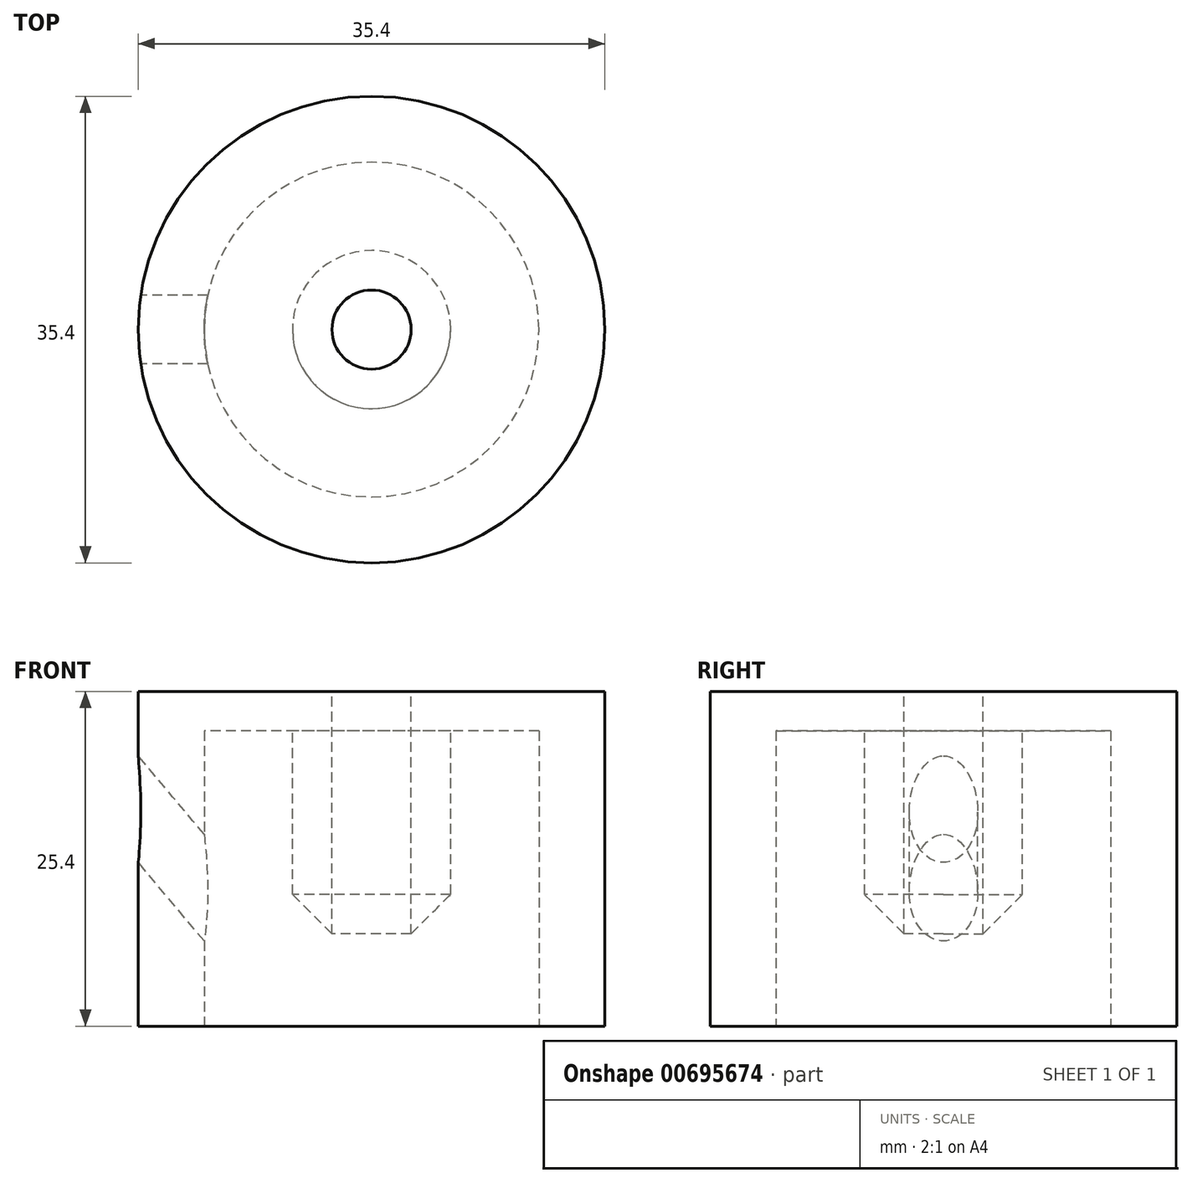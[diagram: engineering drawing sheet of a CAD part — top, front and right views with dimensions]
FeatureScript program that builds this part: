
annotation { "Feature Type Name" : "Feature", "Feature Type Description" : "" }
export const myFeature = defineFeature(function(context is Context, id is Id, definition is map)
    precondition{}
    {
        {
            var Q0;
            Q0=qCreatedBy(makeId("Top.planeOp"),FACE);
            var sketch = newSketch(context, id + "F0", { "sketchPlane" : qUnion([Q0])});
            skCircle(sketch, "E0", {"center": v(0, 0) * mm, "radius": 12.7 * mm});
            skCircle(sketch, "E1", {"center": v(0, 0) * mm, "radius": 17.7 * mm});
            skSolve(sketch);
        }
        {
            var Q0;
            Q0=qSketchRegion(id+"F0",true);
            extrude(context, id + "F1", {"entities" : qUnion([Q0]), "depth" : 25.4 * mm, "offsetDistance" : 25 * mm});
        }
        {
            var Q0;
            Q0=qCreatedBy(makeId("Front.planeOp"),FACE);
            var sketch = newSketch(context, id + "F2", { "sketchPlane" : qUnion([Q0])});
            skLineSegment(sketch, "E2", {"start": v(-34.24, 36.18) * mm, "end": v(-10.1, 7.4) * mm, "construction": true});
            skSolve(sketch);
        }
        {
            var Q0;
            Q0=sQuery(id+"F2.wireOp",EDGE,"E2");
            var Q1;
            Q1=sQuery(id+"F2.wireOp",VERTEX,"E2.start");
            cPlane(context, id + "F3", {"entities" : qUnion([Q0, Q1]), "cplaneType" : CPlaneType.CURVE_POINT, "offset" : 25 * mm, "width" : 150 * mm, "height" : 150 * mm});
        }
        {
            var Q0;
            Q0=qCreatedBy(id+"F3.planeOp",FACE);
            var sketch = newSketch(context, id + "F4", { "sketchPlane" : qUnion([Q0])});
            skCircle(sketch, "E3", {"center": v(-2.97, 0) * mm, "radius": 2.6 * mm});
            skSolve(sketch);
        }
        {
            var Q0;
            Q0=qSketchRegion(id+"F4",true);
            extrude(context, id + "F5", {"entities" : qUnion([Q0]), "operationType" : NewBodyOperationType.REMOVE, "depth" : 38 * mm, "offsetDistance" : 25 * mm});
        }
        {
            var Q0;
            Q0=qCreatedBy(makeId("Front.planeOp"),FACE);
            var sketch = newSketch(context, id + "F6", { "sketchPlane" : qUnion([Q0])});
            skLineSegment(sketch, "E4", {"start": v(0, 87.46) * mm, "end": v(0, -20.33) * mm, "construction": true});
            skSolve(sketch);
        }
        {
            var Q0;
            Q0=makeQuery(id+"F1.opExtrude","CAP_FACE",FACE,{"disambiguationData":[OSD([sQuery(id+"F0.wireOp",EDGE,"E0"),sQuery(id+"F0.wireOp",EDGE,"E1")])],"isStart":true});
            cPlane(context, id + "F7", {"entities" : qUnion([Q0]), "cplaneType" : CPlaneType.OFFSET, "offset" : 10 * mm, "oppositeDirection" : true, "width" : 150 * mm, "height" : 150 * mm});
        }
        {
            var Q0;
            Q0=qCreatedBy(id+"F7.planeOp",FACE);
            var sketch = newSketch(context, id + "F8", { "sketchPlane" : qUnion([Q0])});
            skCircle(sketch, "E5", {"center": v(0, 0) * mm, "radius": 6 * mm});
            skCircle(sketch, "E6", {"center": v(0, 0) * mm, "radius": 3 * mm});
            skSolve(sketch);
        }
        {
            var Q0;
            Q0=qSketchRegion(id+"F8",true);
            extrude(context, id + "F9", {"entities" : qUnion([Q0]), "depth" : 3 * mm, "offsetDistance" : 25 * mm});
        }
        {
            var Q0;
            Q0=makeQuery(id+"F9.opExtrude","CAP_FACE",FACE,{"disambiguationData":[OSD([sQuery(id+"F8.wireOp",EDGE,"E5")])],"isStart":false});
            var sketch = newSketch(context, id + "F10", { "sketchPlane" : qUnion([Q0])});
            skSolve(sketch);
        }
        {
            var Q0;
            Q0=qSketchRegion(id+"F8",true);
            var Q1;
            Q1=makeQuery(id+"F1.opExtrude","CAP_FACE",FACE,{"disambiguationData":[OSD([sQuery(id+"F0.wireOp",EDGE,"E0"),sQuery(id+"F0.wireOp",EDGE,"E1")])],"isStart":false});
            extrude(context, id + "F11", {"entities" : qUnion([Q0]), "operationType" : NewBodyOperationType.ADD, "endBound" : BoundingType.UP_TO_SURFACE, "oppositeDirection" : true, "depth" : 25 * mm, "endBoundEntityFace" : qUnion([Q1]), "offsetDistance" : 25 * mm});
        }
        {
            var Q0;
            Q0=makeQuery(id+"F1.opExtrude","CAP_FACE",FACE,{"disambiguationData":[OSD([sQuery(id+"F0.wireOp",EDGE,"E0"),sQuery(id+"F0.wireOp",EDGE,"E1")])],"isStart":false});
            var sketch = newSketch(context, id + "F12", { "sketchPlane" : qUnion([Q0])});
            skCircle(sketch, "E7", {"center": v(0, 0) * mm, "radius": 17.7 * mm});
            skSolve(sketch);
        }
        {
            var Q0;
            Q0=qSketchRegion(id+"F12",true);
            extrude(context, id + "F13", {"entities" : qUnion([Q0]), "operationType" : NewBodyOperationType.ADD, "oppositeDirection" : true, "depth" : 3 * mm, "offsetDistance" : 25 * mm});
        }
        {
            var Q0;
            Q0=makeQuery(id+"F10.imprint","IMPRINT",FACE,{"disambiguationData":[TD([[makeQuery(id+"F10.imprint","IMPRINT",EDGE,{"derivedFrom":makeQuery(id+"F9.opExtrude","CAP_EDGE",EDGE,{"disambiguationData":[OSD([sQuery(id+"F8.wireOp",EDGE,"E6")])],"isStart":false})}),1.0]])]});
            var sketch = newSketch(context, id + "F14", { "sketchPlane" : qUnion([Q0])});
            skCircle(sketch, "E8", {"center": v(0, 0) * mm, "radius": 3 * mm});
            skSolve(sketch);
        }
        {
            var Q0;
            Q0=qSketchRegion(id+"F14",true);
            extrude(context, id + "F15", {"entities" : qUnion([Q0]), "operationType" : NewBodyOperationType.REMOVE, "endBound" : BoundingType.THROUGH_ALL, "oppositeDirection" : true, "depth" : 25 * mm, "offsetDistance" : 25 * mm});
        }
        {
            var Q0;
            Q0=makeQuery(id+"F9.opExtrude","CAP_EDGE",EDGE,{"disambiguationData":[OSD([sQuery(id+"F8.wireOp",EDGE,"E5")])],"isStart":false});
            chamfer(context, id + "F16", {"entities" : qUnion([Q0]), "width" : 3 * mm, "tangentPropagation" : true});
        }
    });
